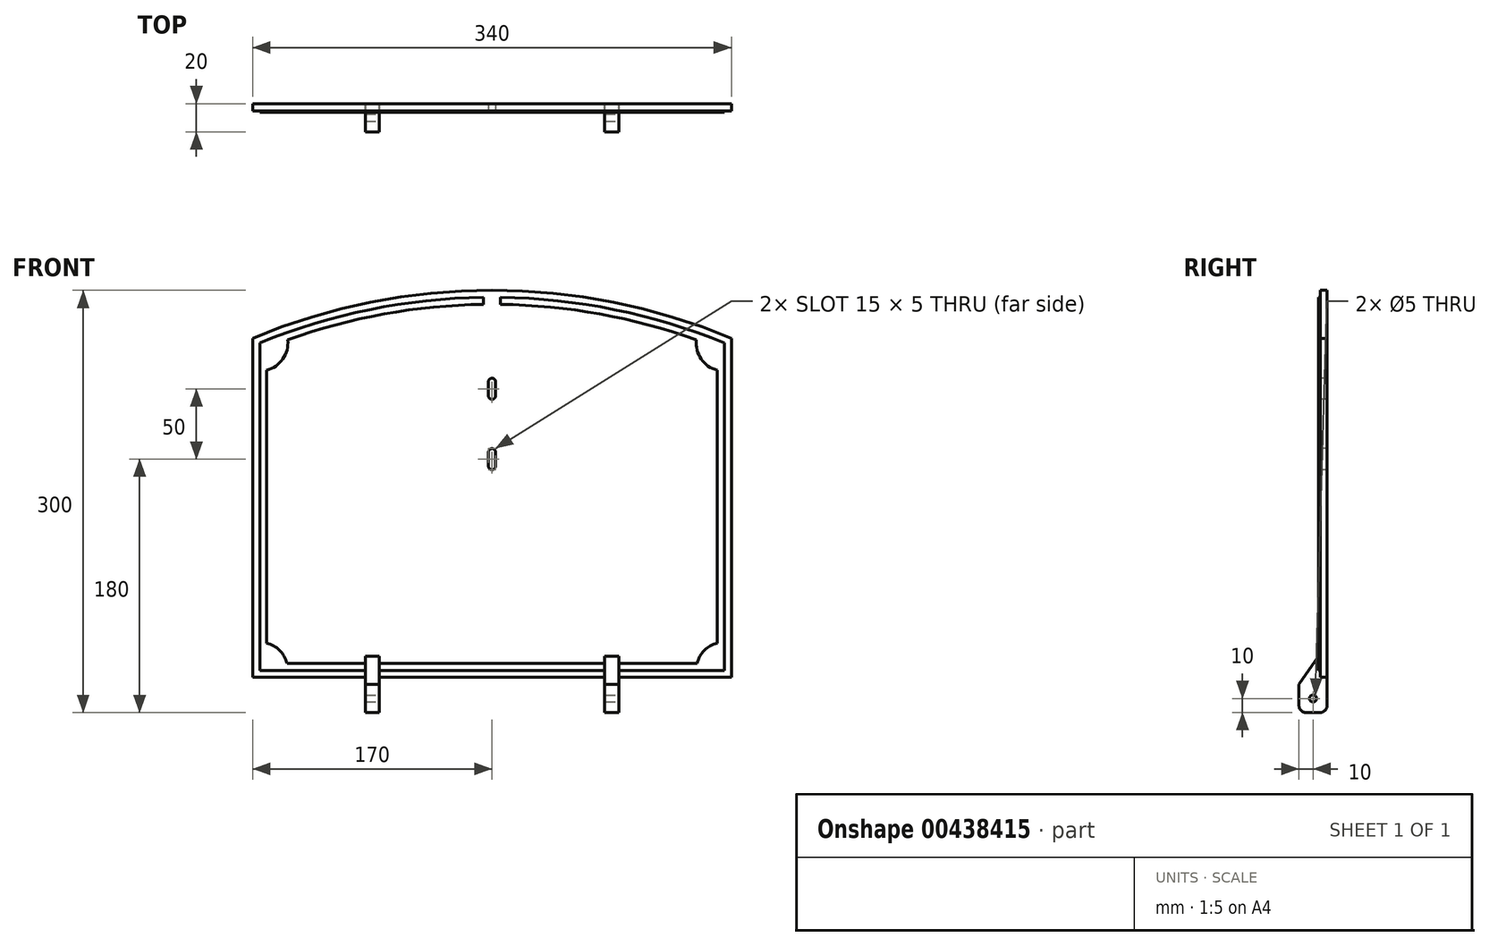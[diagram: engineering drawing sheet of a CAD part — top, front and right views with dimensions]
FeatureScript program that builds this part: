
annotation { "Feature Type Name" : "Feature", "Feature Type Description" : "" }
export const myFeature = defineFeature(function(context is Context, id is Id, definition is map)
    precondition{}
    {
        {
            var Q0;
            Q0=qCreatedBy(makeId("Front.planeOp"),FACE);
            var sketch = newSketch(context, id + "F0", { "sketchPlane" : qUnion([Q0])});
            skLineSegment(sketch, "E0.bottom", {"start": v(155, 107.5) * mm, "end": v(-155, 107.5) * mm, "construction": true});
            skLineSegment(sketch, "E0.top", {"start": v(155, -107.5) * mm, "end": v(-155, -107.5) * mm, "construction": true});
            skLineSegment(sketch, "E0.left", {"start": v(155, 107.5) * mm, "end": v(155, -107.5) * mm, "construction": true});
            skLineSegment(sketch, "E0.right", {"start": v(-155, 107.5) * mm, "end": v(-155, -107.5) * mm, "construction": true});
            skPoint(sketch, "E0.middle", {"position": v(0, 0) * mm});
            skLineSegment(sketch, "E1", {"start": v(0, -107.5) * mm, "end": v(0, 137.5) * mm, "construction": true});
            skPoint(sketch, "E1.endSnap0", {"position": v(0, 107.5) * mm});
            skArc(sketch, "E2", {"start": v(155, 107.5) * mm, "mid": v(0, 137.5) * mm, "end": v(-155, 107.5) * mm, "construction": true});
            skLineSegment(sketch, "E3.0", {"start": v(-140, 102.56) * mm, "end": v(-140, -97.5) * mm, "construction": true});
            skLineSegment(sketch, "E4.0", {"start": v(140, 102.56) * mm, "end": v(140, -97.5) * mm, "construction": true});
            skLineSegment(sketch, "E5.0", {"start": v(140, -97.5) * mm, "end": v(-140, -97.5) * mm, "construction": true});
            skArc(sketch, "E6.0", {"start": v(140, 102.56) * mm, "mid": v(0, 127.5) * mm, "end": v(-140, 102.56) * mm, "construction": true});
            skLineSegment(sketch, "E7.0", {"start": v(-185, 138.23) * mm, "end": v(-185, -137.5) * mm, "construction": true});
            skLineSegment(sketch, "E8.0", {"start": v(185, 138.23) * mm, "end": v(185, -137.5) * mm, "construction": true});
            skLineSegment(sketch, "E9.0", {"start": v(185, -137.5) * mm, "end": v(-185, -137.5) * mm, "construction": true});
            skArc(sketch, "E10.0", {"start": v(185, 138.23) * mm, "mid": v(0, 177.5) * mm, "end": v(-185, 138.23) * mm, "construction": true});
            skLineSegment(sketch, "E11.0", {"start": v(-170, 128.37) * mm, "end": v(-170, -112.5) * mm});
            skArc(sketch, "E11.1", {"start": v(170, 128.37) * mm, "mid": v(0, 162.5) * mm, "end": v(-170, 128.37) * mm});
            skLineSegment(sketch, "E11.2", {"start": v(170, 128.37) * mm, "end": v(170, -112.5) * mm});
            skLineSegment(sketch, "E12.0", {"start": v(170, -112.5) * mm, "end": v(-170, -112.5) * mm});
            skLineSegment(sketch, "E13.bottom", {"start": v(-90, -97.5) * mm, "end": v(-80, -97.5) * mm});
            skLineSegment(sketch, "E13.top", {"start": v(-90, -137.5) * mm, "end": v(-80, -137.5) * mm});
            skLineSegment(sketch, "E13.left", {"start": v(-90, -97.5) * mm, "end": v(-90, -137.5) * mm});
            skLineSegment(sketch, "E13.right", {"start": v(-80, -97.5) * mm, "end": v(-80, -137.5) * mm});
            skLineSegment(sketch, "E14.bottom", {"start": v(80, -97.5) * mm, "end": v(90, -97.5) * mm});
            skLineSegment(sketch, "E14.top", {"start": v(80, -137.5) * mm, "end": v(90, -137.5) * mm});
            skLineSegment(sketch, "E14.left", {"start": v(80, -97.5) * mm, "end": v(80, -137.5) * mm});
            skLineSegment(sketch, "E14.right", {"start": v(90, -97.5) * mm, "end": v(90, -137.5) * mm});
            skSolve(sketch);
        }
        {
            var Q0;
            Q0=makeQuery(id+"F0.imprint","IMPRINT",FACE,{"disambiguationData":[TD([[makeQuery(id+"F0.imprint","IMPRINT",EDGE,{"derivedFrom":sQuery(id+"F0.wireOp",EDGE,"E11.0")}),1.0]])]});
            var Q1;
            {var subQ5=sQuery(id+"F0.wireOp",EDGE,"E13.bottom");Q1=makeQuery(id+"F0.imprint","IMPRINT",FACE,{"disambiguationData":[TD([[makeQuery(id+"F0.imprint","IMPRINT",EDGE,{"derivedFrom":subQ5}),-1.0]])]});}
            var Q2;
            {var subQ5=sQuery(id+"F0.wireOp",EDGE,"E14.bottom");Q2=makeQuery(id+"F0.imprint","IMPRINT",FACE,{"disambiguationData":[TD([[makeQuery(id+"F0.imprint","IMPRINT",EDGE,{"derivedFrom":subQ5}),-1.0]])]});}
            extrude(context, id + "F1", {"entities" : qUnion([Q0, Q1, Q2]), "depth" : 5 * mm});
        }
        {
            var Q0;
            Q0=makeQuery(id+"F1.opExtrude","CAP_FACE",FACE,{"disambiguationData":[OSD([sQuery(id+"F0.wireOp",EDGE,"E11.0"),sQuery(id+"F0.wireOp",EDGE,"E11.1"),sQuery(id+"F0.wireOp",EDGE,"E11.2"),sQuery(id+"F0.wireOp",EDGE,"E12.0")])],"isStart":false});
            var sketch = newSketch(context, id + "F2", { "sketchPlane" : qUnion([Q0])});
            skArc(sketch, "E15.0", {"start": v(170, 128.37) * mm, "mid": v(0, 162.5) * mm, "end": v(-170, 128.37) * mm, "construction": true});
            skLineSegment(sketch, "E16.0.0", {"start": v(-170, -112.5) * mm, "end": v(170, -112.5) * mm, "construction": true});
            skLineSegment(sketch, "E16.0.1", {"start": v(170, -112.5) * mm, "end": v(170, 128.37) * mm, "construction": true});
            skLineSegment(sketch, "E16.0.3", {"start": v(-170, 128.37) * mm, "end": v(-170, -112.5) * mm, "construction": true});
            skLineSegment(sketch, "E17.0", {"start": v(-165, 125.03) * mm, "end": v(-165, -107.5) * mm});
            skArc(sketch, "E17.1", {"start": v(165, 125.03) * mm, "mid": v(87.02, 148.71) * mm, "end": v(6, 157.46) * mm});
            skLineSegment(sketch, "E17.2", {"start": v(165, -107.5) * mm, "end": v(165, 125.03) * mm});
            skLineSegment(sketch, "E17.3", {"start": v(-165, -107.5) * mm, "end": v(165, -107.5) * mm});
            skLineSegment(sketch, "E18.0", {"start": v(160, -88.14) * mm, "end": v(160, 105.66) * mm});
            skLineSegment(sketch, "E18.1", {"start": v(-145.64, -102.5) * mm, "end": v(145.64, -102.5) * mm});
            skLineSegment(sketch, "E18.2", {"start": v(-160, 105.66) * mm, "end": v(-160, -88.14) * mm});
            skArc(sketch, "E18.3", {"start": v(145.13, 127.3) * mm, "mid": v(76.6, 145.63) * mm, "end": v(6, 152.46) * mm});
            skLineSegment(sketch, "E19", {"start": v(0, -112.5) * mm, "end": v(0, 162.5) * mm, "construction": true});
            skArc(sketch, "E20", {"start": v(160, -88.14) * mm, "mid": v(150.86, -93.36) * mm, "end": v(145.64, -102.5) * mm});
            skArc(sketch, "E21.trimOffspring", {"start": v(-160, 105.66) * mm, "mid": v(-148.52, 113.7) * mm, "end": v(-145.13, 127.3) * mm});
            skArc(sketch, "E22.trimOffspring", {"start": v(145.13, 127.3) * mm, "mid": v(148.52, 113.7) * mm, "end": v(160, 105.66) * mm});
            skArc(sketch, "E23.trimOffspring", {"start": v(-145.64, -102.5) * mm, "mid": v(-150.86, -93.36) * mm, "end": v(-160, -88.14) * mm});
            skLineSegment(sketch, "E24", {"start": v(-6, 157.46) * mm, "end": v(-6, 152.46) * mm});
            skLineSegment(sketch, "E25", {"start": v(6, 157.46) * mm, "end": v(6, 152.46) * mm});
            skArc(sketch, "E26.trimOffspring", {"start": v(-6, 157.46) * mm, "mid": v(-87.02, 148.71) * mm, "end": v(-165, 125.03) * mm});
            skArc(sketch, "E27.trimOffspring", {"start": v(-6, 152.46) * mm, "mid": v(-76.6, 145.63) * mm, "end": v(-145.13, 127.3) * mm});
            skSolve(sketch);
        }
        {
            var Q0;
            {var subQ5=sQuery(id+"F2.wireOp",EDGE,"E17.0");Q0=makeQuery(id+"F2.imprint","IMPRINT",FACE,{"disambiguationData":[TD([[makeQuery(id+"F2.imprint","IMPRINT",EDGE,{"derivedFrom":subQ5}),1.0]])]});}
            var Q1;
            {var subQ0=sQuery(id+"F2.wireOp",EDGE,"ZwrtsjM4-WvHo-ftXc-Xm3o-AUTcFLJKpnuq.right");var subQ5=sQuery(id+"F2.wireOp",EDGE,"E18.1");var subQ6=makeQuery(id+"F2.imprint","INTERSECT",VERTEX,{"derivedFrom":[subQ5,subQ0]});Q1=makeQuery(id+"F2.imprint","IMPRINT",FACE,{"disambiguationData":[TD([[makeQuery(id+"F2.imprint","IMPRINT",EDGE,{"disambiguationData":[TD([[subQ6,-1.0]])],"derivedFrom":subQ5}),-1.0]])]});}
            var Q2;
            Q2=makeQuery(id+"F2.imprint","IMPRINT",FACE,{"disambiguationData":[TD([[makeQuery(id+"F2.imprint","IMPRINT",EDGE,{"derivedFrom":sQuery(id+"F2.wireOp",EDGE,"E17.1")}),1.0]])]});
            extrude(context, id + "F3", {"entities" : qUnion([Q0, Q1, Q2]), "operationType" : NewBodyOperationType.ADD, "depth" : 1 * mm});
        }
        {
            var Q0;
            {var subQ5=sQuery(id+"F0.wireOp",EDGE,"E13.top");Q0=makeQuery(id+"F0.imprint","IMPRINT",FACE,{"disambiguationData":[TD([[makeQuery(id+"F0.imprint","IMPRINT",EDGE,{"derivedFrom":subQ5}),1.0]])]});}
            var Q1;
            {var subQ5=sQuery(id+"F0.wireOp",EDGE,"E14.top");Q1=makeQuery(id+"F0.imprint","IMPRINT",FACE,{"disambiguationData":[TD([[makeQuery(id+"F0.imprint","IMPRINT",EDGE,{"derivedFrom":subQ5}),1.0]])]});}
            var Q2;
            {var subQ5=sQuery(id+"F0.wireOp",EDGE,"E14.bottom");Q2=makeQuery(id+"F0.imprint","IMPRINT",FACE,{"disambiguationData":[TD([[makeQuery(id+"F0.imprint","IMPRINT",EDGE,{"derivedFrom":subQ5}),-1.0]])]});}
            var Q3;
            {var subQ5=sQuery(id+"F0.wireOp",EDGE,"E13.bottom");Q3=makeQuery(id+"F0.imprint","IMPRINT",FACE,{"disambiguationData":[TD([[makeQuery(id+"F0.imprint","IMPRINT",EDGE,{"derivedFrom":subQ5}),-1.0]])]});}
            extrude(context, id + "F4", {"entities" : qUnion([Q0, Q1, Q2, Q3]), "operationType" : NewBodyOperationType.ADD, "depth" : 20 * mm});
        }
        {
            var Q0;
            Q0=makeQuery(id+"F4.opExtrude","CAP_EDGE",EDGE,{"disambiguationData":[OSD([sQuery(id+"F0.wireOp",EDGE,"E14.bottom")])],"isStart":false});
            var Q1;
            Q1=makeQuery(id+"F4.opExtrude","CAP_EDGE",EDGE,{"disambiguationData":[OSD([sQuery(id+"F0.wireOp",EDGE,"E13.bottom")])],"isStart":false});
            chamfer(context, id + "F5", {"entities" : qUnion([Q0, Q1]), "chamferType" : ChamferType.TWO_OFFSETS, "width1" : 14 * mm, "oppositeDirection" : false, "width2" : 20 * mm, "tangentPropagation" : true});
        }
        {
            var Q0;
            Q0=makeQuery(id+"F4.opExtrude","CAP_EDGE",EDGE,{"disambiguationData":[OSD([sQuery(id+"F0.wireOp",EDGE,"E13.top")])],"isStart":false});
            var Q1;
            Q1=makeQuery(id+"F4.opExtrude","CAP_EDGE",EDGE,{"disambiguationData":[OSD([sQuery(id+"F0.wireOp",EDGE,"E14.top")])],"isStart":false});
            var Q2;
            Q2=makeQuery(id+"F4.opExtrude","CAP_EDGE",EDGE,{"disambiguationData":[OSD([sQuery(id+"F0.wireOp",EDGE,"E13.top")])],"isStart":true});
            var Q3;
            Q3=makeQuery(id+"F4.opExtrude","CAP_EDGE",EDGE,{"disambiguationData":[OSD([sQuery(id+"F0.wireOp",EDGE,"E14.top")])],"isStart":true});
            fillet(context, id + "F6", {"entities" : qUnion([Q0, Q1, Q2, Q3]), "radius" : 5 * mm, "tangentPropagation" : true, "allowEdgeOverflow" : false});
        }
        {
            var Q0;
            Q0=makeQuery(id+"F4.opExtrude","SWEPT_FACE",FACE,{"disambiguationData":[OSD([sQuery(id+"F0.wireOp",EDGE,"E14.right")])]});
            var sketch = newSketch(context, id + "F7", { "sketchPlane" : qUnion([Q0])});
            skCircle(sketch, "E28", {"center": v(-10, -127.5) * mm, "radius": 2.5 * mm});
            skSolve(sketch);
        }
        {
            var Q0;
            Q0=sQuery(id+"F7.wireOp",VERTEX,"E28.center");
            var Q1;
            Q1=makeQuery(id+"F1.opExtrude","SWEPT_BODY",BODY,{"disambiguationData":[OSD([sQuery(id+"F0.wireOp",EDGE,"E11.0"),sQuery(id+"F0.wireOp",EDGE,"E11.1"),sQuery(id+"F0.wireOp",EDGE,"E11.2"),sQuery(id+"F0.wireOp",EDGE,"E12.0")])]});
            hole(context, id + "F8", {"style" : HoleStyle.SIMPLE, "endStyle" : HoleEndStyle.THROUGH, "holeDiameter" : 5 * mm, "isTappedThrough" : true, "tappedDepth" : 12 * mm, "tapClearance" : 3, "locations" : qUnion([Q0]), "scope" : qUnion([Q1])});
        }
        {
            var Q0;
            {var subQ0=sQuery(id+"F0.wireOp",EDGE,"E11.1");var subQ1=sQuery(id+"F0.wireOp",EDGE,"E12.0");var subQ2=sQuery(id+"F0.wireOp",EDGE,"E11.0");var subQ3=sQuery(id+"F0.wireOp",EDGE,"E11.2");Q0=makeQuery(id+"F4.boolean.opBoolean","SPLIT",FACE,{"disambiguationData":[TD([makeQuery(id+"F1.opExtrude","SWEPT_FACE",FACE,{"disambiguationData":[OSD([subQ2])]}),makeQuery(id+"F1.opExtrude","SWEPT_FACE",FACE,{"disambiguationData":[OSD([subQ0])]}),makeQuery(id+"F1.opExtrude","SWEPT_FACE",FACE,{"disambiguationData":[OSD([subQ3])]}),makeQuery(id+"F1.opExtrude","SWEPT_FACE",FACE,{"disambiguationData":[OSD([subQ1])]}),makeQuery(id+"F3.opExtrude","SWEPT_FACE",FACE,{"disambiguationData":[OSD([sQuery(id+"F2.wireOp",EDGE,"E17.0")])]}),makeQuery(id+"F3.opExtrude","SWEPT_FACE",FACE,{"disambiguationData":[OSD([sQuery(id+"F2.wireOp",EDGE,"E17.1")])]}),makeQuery(id+"F3.opExtrude","SWEPT_FACE",FACE,{"disambiguationData":[OSD([sQuery(id+"F2.wireOp",EDGE,"E17.2")])]}),makeQuery(id+"F3.opExtrude","SWEPT_FACE",FACE,{"disambiguationData":[OSD([sQuery(id+"F2.wireOp",EDGE,"E17.3")])]}),makeQuery(id+"F3.opExtrude","SWEPT_FACE",FACE,{"disambiguationData":[OSD([sQuery(id+"F2.wireOp",EDGE,"E18.0")])]}),makeQuery(id+"F3.opExtrude","SWEPT_FACE",FACE,{"disambiguationData":[OSD([sQuery(id+"F2.wireOp",EDGE,"E18.1")])]}),makeQuery(id+"F3.opExtrude","SWEPT_FACE",FACE,{"disambiguationData":[OSD([sQuery(id+"F2.wireOp",EDGE,"E18.2")])]}),makeQuery(id+"F3.opExtrude","SWEPT_FACE",FACE,{"disambiguationData":[OSD([sQuery(id+"F2.wireOp",EDGE,"E18.3")])]}),makeQuery(id+"F3.opExtrude","SWEPT_FACE",FACE,{"disambiguationData":[OSD([sQuery(id+"F2.wireOp",EDGE,"E20")])]}),makeQuery(id+"F3.opExtrude","SWEPT_FACE",FACE,{"disambiguationData":[OSD([sQuery(id+"F2.wireOp",EDGE,"E21.trimOffspring")])]}),makeQuery(id+"F3.opExtrude","SWEPT_FACE",FACE,{"disambiguationData":[OSD([sQuery(id+"F2.wireOp",EDGE,"E22.trimOffspring")])]}),makeQuery(id+"F3.opExtrude","SWEPT_FACE",FACE,{"disambiguationData":[OSD([sQuery(id+"F2.wireOp",EDGE,"E23.trimOffspring")])]}),makeQuery(id+"F3.opExtrude","SWEPT_FACE",FACE,{"disambiguationData":[OSD([sQuery(id+"F2.wireOp",EDGE,"E24")])]}),makeQuery(id+"F3.opExtrude","SWEPT_FACE",FACE,{"disambiguationData":[OSD([sQuery(id+"F2.wireOp",EDGE,"E25")])]}),makeQuery(id+"F3.opExtrude","SWEPT_FACE",FACE,{"disambiguationData":[OSD([sQuery(id+"F2.wireOp",EDGE,"E26.trimOffspring")])]}),makeQuery(id+"F3.opExtrude","SWEPT_FACE",FACE,{"disambiguationData":[OSD([sQuery(id+"F2.wireOp",EDGE,"E27.trimOffspring")])]}),makeQuery(id+"F4.opExtrude","SWEPT_FACE",FACE,{"disambiguationData":[OSD([sQuery(id+"F0.wireOp",EDGE,"E13.bottom")])]}),makeQuery(id+"F4.opExtrude","SWEPT_FACE",FACE,{"disambiguationData":[OSD([sQuery(id+"F0.wireOp",EDGE,"E13.left")])]}),makeQuery(id+"F4.opExtrude","SWEPT_FACE",FACE,{"disambiguationData":[OSD([sQuery(id+"F0.wireOp",EDGE,"E13.right")])]}),makeQuery(id+"F4.opExtrude","SWEPT_FACE",FACE,{"disambiguationData":[OSD([sQuery(id+"F0.wireOp",EDGE,"E14.bottom")])]}),makeQuery(id+"F4.opExtrude","SWEPT_FACE",FACE,{"disambiguationData":[OSD([sQuery(id+"F0.wireOp",EDGE,"E14.left")])]}),makeQuery(id+"F4.opExtrude","SWEPT_FACE",FACE,{"disambiguationData":[OSD([sQuery(id+"F0.wireOp",EDGE,"E14.right")])]})])],"derivedFrom":makeQuery(id+"F1.opExtrude","CAP_FACE",FACE,{"disambiguationData":[OSD([subQ2,subQ0,subQ3,subQ1])],"isStart":false})});}
            var sketch = newSketch(context, id + "F9", { "sketchPlane" : qUnion([Q0])});
            skLineSegment(sketch, "E29.0", {"start": v(80, -112.5) * mm, "end": v(-80, -112.5) * mm, "construction": true});
            skLineSegment(sketch, "E30", {"start": v(0, -112.5) * mm, "end": v(0, 162.5) * mm, "construction": true});
            skArc(sketch, "E31", {"start": v(2.5, 97.5) * mm, "mid": v(0, 100) * mm, "end": v(-2.5, 97.5) * mm});
            skArc(sketch, "E32", {"start": v(-2.5, 87.5) * mm, "mid": v(0, 85) * mm, "end": v(2.5, 87.5) * mm});
            skArc(sketch, "E33", {"start": v(2.5, 47.5) * mm, "mid": v(0, 50) * mm, "end": v(-2.5, 47.5) * mm});
            skArc(sketch, "E34", {"start": v(-2.5, 37.5) * mm, "mid": v(0, 35) * mm, "end": v(2.5, 37.5) * mm});
            skLineSegment(sketch, "E35", {"start": v(2.5, 97.5) * mm, "end": v(2.5, 87.5) * mm});
            skLineSegment(sketch, "E36", {"start": v(-2.5, 97.5) * mm, "end": v(-2.5, 87.5) * mm});
            skLineSegment(sketch, "E37", {"start": v(2.5, 47.5) * mm, "end": v(2.5, 37.5) * mm});
            skLineSegment(sketch, "E38", {"start": v(-2.5, 47.5) * mm, "end": v(-2.5, 37.5) * mm});
            skSolve(sketch);
        }
        {
            var Q0;
            Q0=makeQuery(id+"F9.imprint","IMPRINT",FACE,{"disambiguationData":[TD([[makeQuery(id+"F9.imprint","IMPRINT",EDGE,{"derivedFrom":sQuery(id+"F9.wireOp",EDGE,"E31")}),1.0]])]});
            var Q1;
            Q1=makeQuery(id+"F9.imprint","IMPRINT",FACE,{"disambiguationData":[TD([[makeQuery(id+"F9.imprint","IMPRINT",EDGE,{"derivedFrom":sQuery(id+"F9.wireOp",EDGE,"E33")}),1.0]])]});
            extrude(context, id + "F10", {"entities" : qUnion([Q0, Q1]), "operationType" : NewBodyOperationType.REMOVE, "oppositeDirection" : true, "depth" : 5 * mm});
        }
    });
